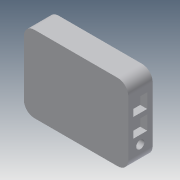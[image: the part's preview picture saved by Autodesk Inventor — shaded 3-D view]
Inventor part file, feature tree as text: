
AUTODESK INVENTOR PART (.ipt)
format: ipt  version: 2014 (Build 180170000, 170)  size: 116,224 bytes
history: native  units: in
note: dims shown in document units (in); Inventor stores cm internally (conversion verified against a paired STEP export)
features: extrude x3, sketch x3
ambient origin geometry x8: Origin, YZ Plane, XZ Plane, XY Plane, X Axis, Y Axis, Z Axis, Center Point
bodies: Solid1 (feature_tree)
feature tree (6):
  extrude  "Extrusion1"  Depth=2.75in
  extrude  "Extrusion2"  Depth=0.875in TaperAngle=0.0deg
  extrude  "Extrusion3"  Depth=0.375in
  sketch  "Sketch1"  dims[d0=3.75in d1=2.75in]
  sketch  "Sketch2"  dims[d2=0.375in d3=0.875in d4=0.0in]
  sketch  "Sketch3"  dims[d5=0.25in d6=0.0in d7=0.375in d8=0.375in d9=0.375in d10=0.375in d11=0.125in d12=0.0in]
